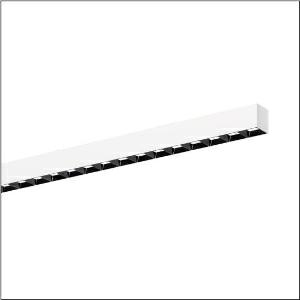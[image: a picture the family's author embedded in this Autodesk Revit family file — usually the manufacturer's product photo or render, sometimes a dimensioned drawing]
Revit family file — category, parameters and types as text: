
# Revit family: silica_r__21_51mx24da34wb_1271
name_source: partatom
category: Lighting Fixtures
units: mm (PartAtom-declared; Revit-internal decimal feet)

## family parameters
Cut with Voids When Loaded = No
Host = Face
Light Source = No
Part Type = Normal
Room Calculation Point = No
Round Connector Dimension = Use Diameter
Shared = No

## types (1)
- --- (1 x LED, 4320 lm, 32.1 W, 3000K)
    Apparent Load = 32 VA
    CIE Flux Codes = 74 94 99 100 100
    Color Rendering = 80
    Color Temperature = 3000K
    Default Elevation = 1800 mm
    Description = Silica® 21, office luminaire, primary light control with darklight reflector, of PMMA, black, CAT 2 (L<= 3000cd/m²), light emission: direct distribution, primary light characteristic: asymmetric, installation type: surface-mounted, LED, rated luminous flux: 4.320lm, luminous efficacy: 135lm/W, light colour: 830, colour temperature: 3000K, with terminal, 3+2-pole, max. 2.5mm², mains connection: 220..240V, AC, 50/60Hz, rated input power: 32.1W, luminaire housing, of aluminium, traffic white (RAL 9016), length: 1.204mm, width: 53mm, height: 53mm, protection rating (complete): IP20, insulation class (complete): insulation class I (protective earthing), certification: CE, permissible operating ambient temperature: 0..+35°C, standard: EN 50419, packaging unit: 1 piece
    Height = 0 mm  [stored 0 ft]
    Lamp = 1 x LED
    Lamp Light Flux = 4320 lm
    Lamp Power = 32.1 W
    Lamp count = 1
    Length = 1204 mm
    Luminous efficacy = 135 lm/W
    Manufacturer = Siteco
    ModVariant = No
    Model = 51MX24DA34WB
    Mounting Place = Ceiling
    Mounting Type = Recessed
    Number of Poles = 1
    OnlyDefault = Yes
    Power Factor = 1
    Product Name = Silica® 21
    Product group = office luminaire | ceiling recessed
    ProductGroupID = 401
    Protection Class = Protection class I
    Protection Degree = IP 20
    RLX_Detail_Level = 1
    RLX_Emergency_Light_Flux = 0 lm
    RLX_Emergency_Type = 0
    RLX_Emergency_Type_DB = No
    RlxData = <blob elided: 41469 chars, md5=37ac773a>
    Socket = socket
    Standby Power = 0 W
    System Light Flux = 4320 lm
    System Power = 32 W
    Type Comments = factory setting: luminous flux: 100 % | dim-lin: 254 | 448 mA
    Type Image = l_1313592.jpg
    URL = http://relux.com
    VarID = @adj_072097
    Voltage = 0 V
    Weight = 0.00 kg
    Width = 53 mm

note: [stored X ft] marks values corroborated as IEEE doubles in the binary element streams (Revit-internal decimal feet)

## geometry (parser evidence)
native form markers: Blend x4, Sweep x10
no freeform markers — native parametric forms only
